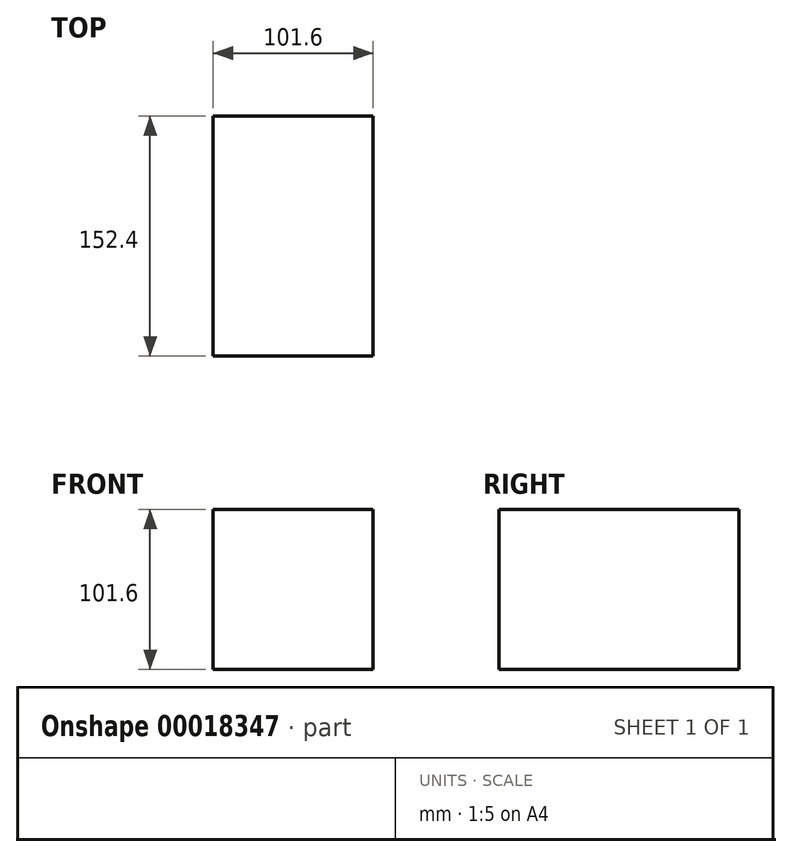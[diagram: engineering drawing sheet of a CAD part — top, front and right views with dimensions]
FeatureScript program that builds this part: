
annotation { "Feature Type Name" : "Feature", "Feature Type Description" : "" }
export const myFeature = defineFeature(function(context is Context, id is Id, definition is map)
    precondition{}
    {
        {
            var Q0;
            Q0=qCreatedBy(makeId("Front.planeOp"),FACE);
            var sketch = newSketch(context, id + "F0", { "sketchPlane" : qUnion([Q0])});
            skLineSegment(sketch, "E0.rect.bottom", {"start": v(-50.8, 50.8) * mm, "end": v(50.8, 50.8) * mm});
            skLineSegment(sketch, "E0.rect.top", {"start": v(-50.8, -50.8) * mm, "end": v(50.8, -50.8) * mm});
            skLineSegment(sketch, "E0.rect.left", {"start": v(-50.8, 50.8) * mm, "end": v(-50.8, -50.8) * mm});
            skLineSegment(sketch, "E0.rect.right", {"start": v(50.8, 50.8) * mm, "end": v(50.8, -50.8) * mm});
            skPoint(sketch, "E0.rect.middle", {"position": v(0, 0) * mm});
            skSolve(sketch);
        }
        {
            var Q0;
            Q0=makeQuery(id+"F0.imprint","IMPRINT",FACE,{"disambiguationData":[TD([[makeQuery(id+"F0.imprint","IMPRINT",EDGE,{"derivedFrom":sQuery(id+"F0.wireOp",EDGE,"E0.rect.bottom")}),-1.0]])]});
            extrude(context, id + "F1", {"entities" : qUnion([Q0]), "endBound" : BoundingType.SYMMETRIC, "depth" : 101.6 * mm});
        }
        {
            var Q0;
            Q0=makeQuery(id+"F1.opExtrude","CAP_FACE",FACE,{"disambiguationData":[OSD([sQuery(id+"F0.wireOp",EDGE,"E0.rect.bottom"),sQuery(id+"F0.wireOp",EDGE,"E0.rect.top"),sQuery(id+"F0.wireOp",EDGE,"E0.rect.left"),sQuery(id+"F0.wireOp",EDGE,"E0.rect.right")])],"isStart":false});
            var sketch = newSketch(context, id + "F2", { "sketchPlane" : qUnion([Q0])});
            skLineSegment(sketch, "E1.rect.bottom", {"start": v(-50.8, 50.8) * mm, "end": v(50.8, 50.8) * mm});
            skLineSegment(sketch, "E1.rect.top", {"start": v(-50.8, -50.8) * mm, "end": v(50.8, -50.8) * mm});
            skLineSegment(sketch, "E1.rect.left", {"start": v(-50.8, 50.8) * mm, "end": v(-50.8, -50.8) * mm});
            skLineSegment(sketch, "E1.rect.right", {"start": v(50.8, 50.8) * mm, "end": v(50.8, -50.8) * mm});
            skPoint(sketch, "E1.rect.middle", {"position": v(0, 0) * mm});
            skSolve(sketch);
        }
        {
            var Q0;
            Q0=makeQuery(id+"F2.imprint","IMPRINT",FACE,{"disambiguationData":[TD([[makeQuery(id+"F2.imprint","IMPRINT",EDGE,{"derivedFrom":sQuery(id+"F2.wireOp",EDGE,"E1.rect.bottom")}),-1.0]])]});
            extrude(context, id + "F3", {"entities" : qUnion([Q0]), "operationType" : NewBodyOperationType.ADD, "endBound" : BoundingType.SYMMETRIC, "depth" : 101.6 * mm});
        }
    });
